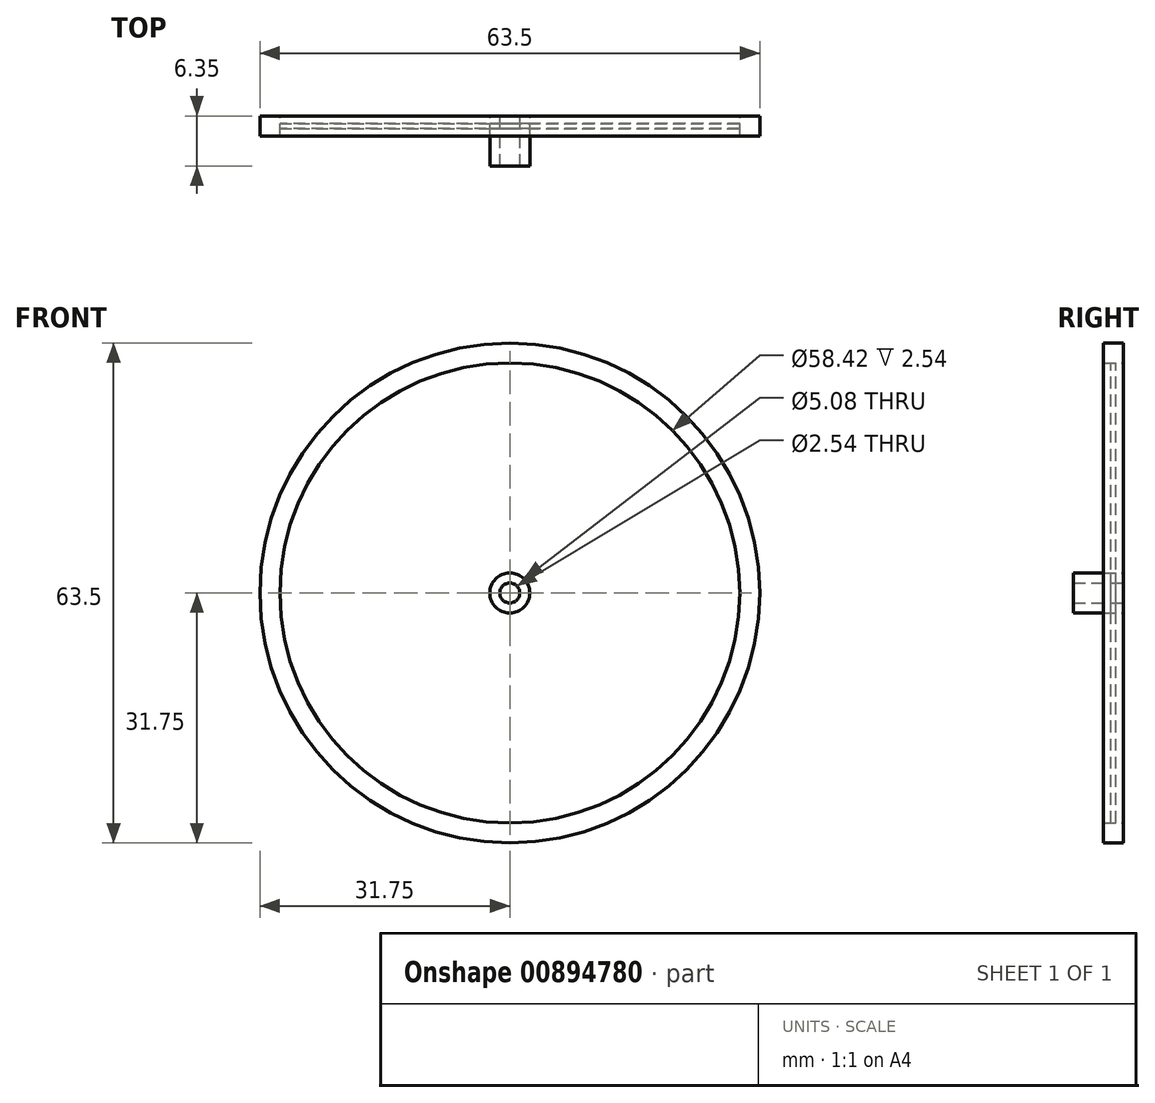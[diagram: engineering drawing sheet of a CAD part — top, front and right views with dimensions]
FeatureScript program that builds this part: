
annotation { "Feature Type Name" : "Feature", "Feature Type Description" : "" }
export const myFeature = defineFeature(function(context is Context, id is Id, definition is map)
    precondition{}
    {
        {
            var Q0;
            Q0=qCreatedBy(makeId("Front.planeOp"),FACE);
            var sketch = newSketch(context, id + "F0", { "sketchPlane" : qUnion([Q0])});
            skCircle(sketch, "E0", {"center": v(0, 0) * mm, "radius": 31.75 * mm});
            skCircle(sketch, "E1", {"center": v(0, 0) * mm, "radius": 29.21 * mm});
            skCircle(sketch, "E2", {"center": v(0, 0) * mm, "radius": 2.54 * mm});
            skCircle(sketch, "E3", {"center": v(0, 0) * mm, "radius": 1.27 * mm});
            skSolve(sketch);
        }
        {
            var Q0;
            Q0=makeQuery(id+"F0.imprint","IMPRINT",FACE,{"disambiguationData":[TD([[makeQuery(id+"F0.imprint","IMPRINT",EDGE,{"derivedFrom":sQuery(id+"F0.wireOp",EDGE,"E2")}),1.0]])]});
            extrude(context, id + "F1", {"entities" : qUnion([Q0]), "depth" : 5.08 * mm, "offsetDistance" : 25.4 * mm, "hasSecondDirection" : true, "secondDirectionOppositeDirection" : true, "secondDirectionDepth" : 1.27 * mm});
        }
        {
            var Q0;
            Q0 = qSketchRegion(id + "F0", true);
            extrude(context, id + "F2", {"entities" : qUnion([Q0]), "depth" : 1.27 * mm, "offsetDistance" : 25.4 * mm, "hasSecondDirection" : true, "secondDirectionOppositeDirection" : true, "secondDirectionDepth" : 1.27 * mm});
        }
        {
            var Q0;
            Q0=makeQuery(id+"F0.imprint","IMPRINT",FACE,{"disambiguationData":[TD([[makeQuery(id+"F0.imprint","IMPRINT",EDGE,{"derivedFrom":sQuery(id+"F0.wireOp",EDGE,"E1")}),1.0]])]});
            extrude(context, id + "F3", {"entities" : qUnion([Q0]), "depth" : 0.32 * mm, "offsetDistance" : 25.4 * mm, "hasSecondDirection" : true, "secondDirectionOppositeDirection" : true, "secondDirectionDepth" : 0.32 * mm});
        }
    });
